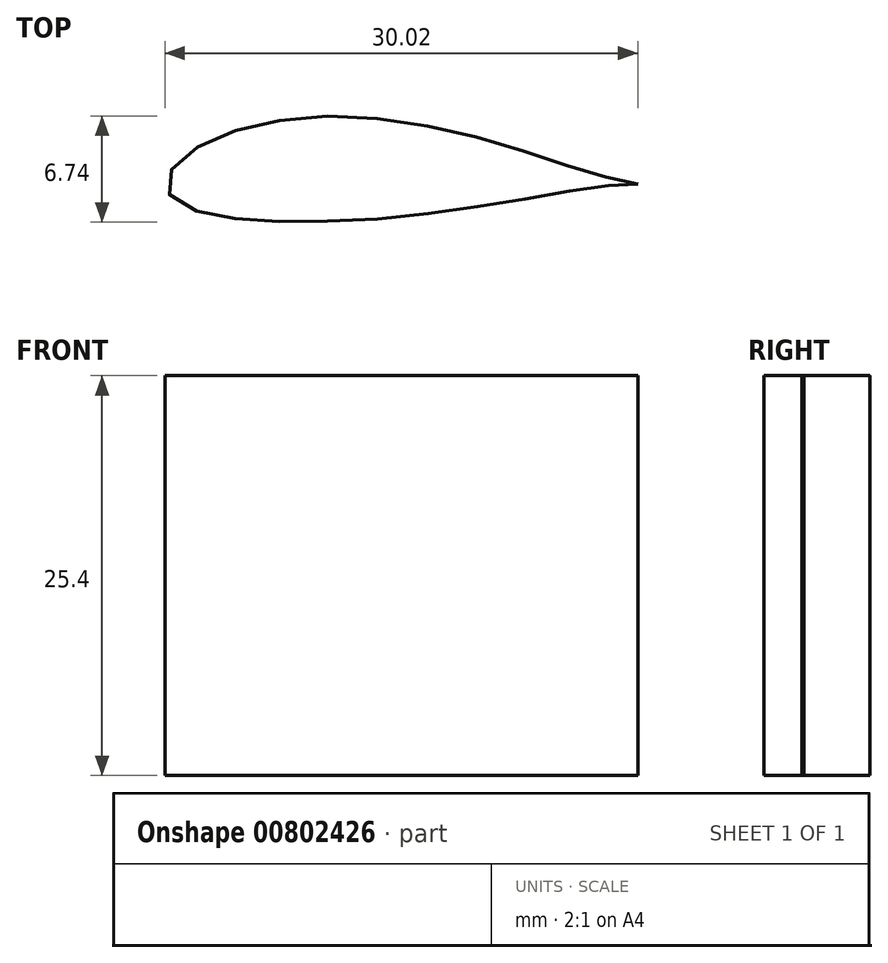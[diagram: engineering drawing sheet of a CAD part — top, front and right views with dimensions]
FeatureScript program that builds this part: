
annotation { "Feature Type Name" : "Feature", "Feature Type Description" : "" }
export const myFeature = defineFeature(function(context is Context, id is Id, definition is map)
    precondition{}
    {
        {
            var Q0;
            Q0=qCreatedBy(makeId("Top.planeOp"),FACE);
            var sketch = newSketch(context, id + "F0", { "sketchPlane" : qUnion([Q0])});
            skPoint(sketch, "E0", {"position": v(-10, 0) * mm});
            skPoint(sketch, "E1", {"position": v(-9.84, 0.56) * mm});
            skPoint(sketch, "E2", {"position": v(-9.94, 0.25) * mm});
            skPoint(sketch, "E3", {"position": v(-9.67, 0.85) * mm});
            skPoint(sketch, "E4", {"position": v(-9.46, 1.15) * mm});
            skPoint(sketch, "E5", {"position": v(-9.18, 1.45) * mm});
            skPoint(sketch, "E6", {"position": v(-8.82, 1.76) * mm});
            skPoint(sketch, "E7", {"position": v(-8.42, 2.06) * mm});
            skPoint(sketch, "E8", {"position": v(-7.96, 2.36) * mm});
            skPoint(sketch, "E9", {"position": v(-7.44, 2.63) * mm});
            skPoint(sketch, "E10", {"position": v(-6.86, 2.9) * mm});
            skPoint(sketch, "E11", {"position": v(-6.24, 3.16) * mm});
            skPoint(sketch, "E12", {"position": v(-5.55, 3.4) * mm});
            skPoint(sketch, "E13", {"position": v(-4.86, 3.6) * mm});
            skPoint(sketch, "E14", {"position": v(-4.1, 3.78) * mm});
            skPoint(sketch, "E15", {"position": v(-3.31, 3.93) * mm});
            skPoint(sketch, "E16", {"position": v(-2.48, 4.07) * mm});
            skPoint(sketch, "E17", {"position": v(-1.6, 4.18) * mm});
            skPoint(sketch, "E18", {"position": v(-0.7, 4.3) * mm});
            skPoint(sketch, "E19", {"position": v(0.21, 4.3) * mm});
            skPoint(sketch, "E20", {"position": v(1.16, 4.3) * mm});
            skPoint(sketch, "E21", {"position": v(-10, -0.27) * mm});
            skPoint(sketch, "E22", {"position": v(-9.83, -0.52) * mm});
            skPoint(sketch, "E23", {"position": v(-9.68, -0.75) * mm});
            skPoint(sketch, "E24", {"position": v(-9.46, -1) * mm});
            skPoint(sketch, "E25", {"position": v(-9.16, -1.22) * mm});
            skPoint(sketch, "E26", {"position": v(-8.82, -1.4) * mm});
            skPoint(sketch, "E27", {"position": v(-8.42, -1.6) * mm});
            skPoint(sketch, "E28", {"position": v(-7.94, -1.74) * mm});
            skPoint(sketch, "E29", {"position": v(-7.44, -1.88) * mm});
            skPoint(sketch, "E30", {"position": v(-6.85, -2.03) * mm});
            skPoint(sketch, "E31", {"position": v(-6.25, -2.14) * mm});
            skPoint(sketch, "E32", {"position": v(-5.56, -2.2) * mm});
            skPoint(sketch, "E33", {"position": v(-4.86, -2.27) * mm});
            skPoint(sketch, "E34", {"position": v(-4.1, -2.35) * mm});
            skPoint(sketch, "E35", {"position": v(1.16, -2.34) * mm});
            skPoint(sketch, "E36", {"position": v(2.1, -2.29) * mm});
            skPoint(sketch, "E37", {"position": v(4.04, 4.1) * mm});
            skPoint(sketch, "E38", {"position": v(5.04, 3.98) * mm});
            skPoint(sketch, "E39", {"position": v(6.02, 3.78) * mm});
            skPoint(sketch, "E40", {"position": v(3.08, -2.24) * mm});
            skPoint(sketch, "E41", {"position": v(4.06, -2.17) * mm});
            skPoint(sketch, "E42", {"position": v(5.04, -2.08) * mm});
            skPoint(sketch, "E43", {"position": v(6.02, -1.96) * mm});
            skPoint(sketch, "E44", {"position": v(7.02, -1.85) * mm});
            skPoint(sketch, "E45", {"position": v(7.95, -1.71) * mm});
            skPoint(sketch, "E46", {"position": v(8.91, -1.6) * mm});
            skPoint(sketch, "E47", {"position": v(9.87, -1.44) * mm});
            skPoint(sketch, "E48", {"position": v(10.78, -1.3) * mm});
            skPoint(sketch, "E49", {"position": v(11.67, -1.12) * mm});
            skPoint(sketch, "E50", {"position": v(12.53, -1) * mm});
            skPoint(sketch, "E51", {"position": v(7.02, 3.62) * mm});
            skPoint(sketch, "E52", {"position": v(7.95, 3.44) * mm});
            skPoint(sketch, "E53", {"position": v(8.93, 3.21) * mm});
            skPoint(sketch, "E54", {"position": v(9.85, 2.96) * mm});
            skPoint(sketch, "E55", {"position": v(10.76, 2.69) * mm});
            skPoint(sketch, "E56", {"position": v(11.67, 2.41) * mm});
            skPoint(sketch, "E57", {"position": v(12.53, 2.18) * mm});
            skPoint(sketch, "E58", {"position": v(13.38, 1.87) * mm});
            skPoint(sketch, "E59", {"position": v(14.15, 1.64) * mm});
            skPoint(sketch, "E60", {"position": v(13.35, -0.85) * mm});
            skPoint(sketch, "E61", {"position": v(14.16, -0.7) * mm});
            skPoint(sketch, "E62", {"position": v(14.93, -0.59) * mm});
            skPoint(sketch, "E63", {"position": v(15.62, -0.46) * mm});
            skPoint(sketch, "E64", {"position": v(16.28, -0.35) * mm});
            skPoint(sketch, "E65", {"position": v(16.93, -0.25) * mm});
            skPoint(sketch, "E66", {"position": v(17.5, -0.17) * mm});
            skPoint(sketch, "E67", {"position": v(18.01, -0.11) * mm});
            skPoint(sketch, "E68", {"position": v(20, 0) * mm});
            skPoint(sketch, "E69", {"position": v(19.88, 0) * mm});
            skPoint(sketch, "E70", {"position": v(19.72, 0) * mm});
            skPoint(sketch, "E71", {"position": v(19.52, 0) * mm});
            skPoint(sketch, "E72", {"position": v(19.2, 0) * mm});
            skPoint(sketch, "E73", {"position": v(18.47, -0.06) * mm});
            skPoint(sketch, "E74", {"position": v(18.86, -0.03) * mm});
            skPoint(sketch, "E75", {"position": v(18.86, 0.21) * mm});
            skPoint(sketch, "E76", {"position": v(19.2, 0.13) * mm});
            skPoint(sketch, "E77", {"position": v(18.47, 0.31) * mm});
            skPoint(sketch, "E78", {"position": v(19.5, 0.08) * mm});
            skPoint(sketch, "E79", {"position": v(19.72, 0.03) * mm});
            skPoint(sketch, "E80", {"position": v(19.88, 0.02) * mm});
            skPoint(sketch, "E81", {"position": v(14.9, 1.38) * mm});
            skPoint(sketch, "E82", {"position": v(15.62, 1.15) * mm});
            skPoint(sketch, "E83", {"position": v(16.28, 0.94) * mm});
            skPoint(sketch, "E84", {"position": v(16.9, 0.75) * mm});
            skPoint(sketch, "E85", {"position": v(17.5, 0.58) * mm});
            skPoint(sketch, "E86", {"position": v(18.01, 0.43) * mm});
            skPoint(sketch, "E87", {"position": v(2.1, 4.26) * mm});
            skPoint(sketch, "E88", {"position": v(3.07, 4.2) * mm});
            skPoint(sketch, "E89", {"position": v(0.2, -2.37) * mm});
            skPoint(sketch, "E90", {"position": v(-3.32, -2.37) * mm});
            skPoint(sketch, "E91", {"position": v(-2.47, -2.4) * mm});
            skPoint(sketch, "E92", {"position": v(-1.6, -2.41) * mm});
            skPoint(sketch, "E93", {"position": v(-0.7, -2.41) * mm});
            skFitSpline(sketch, "E94", {"points": [v(20, 0) * mm, v(19.88, 0.02) * mm, v(19.52, 0) * mm, v(19.2, 0) * mm, v(18.86, -0.03) * mm, v(18.47, -0.06) * mm, v(18.01, -0.11) * mm, v(17.5, -0.17) * mm, v(16.93, -0.25) * mm, v(16.28, -0.35) * mm, v(15.62, -0.46) * mm, v(14.93, -0.59) * mm, v(14.16, -0.7) * mm, v(13.35, -0.85) * mm, v(12.53, -1) * mm, v(11.67, -1.12) * mm, v(10.78, -1.3) * mm, v(9.87, -1.44) * mm, v(8.91, -1.6) * mm, v(7.95, -1.71) * mm, v(7.02, -1.85) * mm, v(6.02, -1.96) * mm, v(5.04, -2.08) * mm, v(4.06, -2.17) * mm, v(3.08, -2.24) * mm, v(2.1, -2.29) * mm, v(1.16, -2.34) * mm, v(0.2, -2.37) * mm, v(-0.7, -2.41) * mm, v(-1.6, -2.41) * mm, v(-2.47, -2.4) * mm, v(-3.32, -2.37) * mm, v(-4.1, -2.35) * mm, v(-4.86, -2.27) * mm, v(-5.56, -2.2) * mm, v(-6.25, -2.14) * mm, v(-6.85, -2.03) * mm, v(-7.44, -1.88) * mm, v(-7.94, -1.74) * mm, v(-8.42, -1.6) * mm, v(-8.82, -1.4) * mm, v(-9.16, -1.22) * mm, v(-9.46, -1) * mm, v(-9.68, -0.75) * mm, v(-9.83, -0.52) * mm, v(-10, -0.27) * mm, v(-10, 0) * mm, v(-9.94, 0.25) * mm, v(-9.84, 0.56) * mm, v(-9.67, 0.85) * mm, v(-9.46, 1.15) * mm, v(-9.18, 1.45) * mm, v(-8.82, 1.76) * mm, v(-8.42, 2.06) * mm, v(-7.96, 2.36) * mm, v(-7.44, 2.63) * mm, v(-6.86, 2.9) * mm, v(-6.24, 3.16) * mm, v(-5.55, 3.4) * mm, v(-4.86, 3.6) * mm, v(-4.1, 3.78) * mm, v(-3.31, 3.93) * mm, v(-2.48, 4.07) * mm, v(-1.6, 4.18) * mm, v(-0.7, 4.3) * mm, v(0.21, 4.3) * mm, v(1.16, 4.3) * mm, v(2.1, 4.26) * mm, v(3.07, 4.2) * mm, v(4.04, 4.1) * mm, v(5.04, 3.98) * mm, v(6.02, 3.78) * mm, v(7.02, 3.62) * mm, v(7.95, 3.44) * mm, v(8.93, 3.21) * mm, v(9.85, 2.96) * mm, v(10.76, 2.69) * mm, v(11.67, 2.41) * mm, v(12.53, 2.18) * mm, v(13.38, 1.87) * mm, v(14.15, 1.64) * mm, v(14.9, 1.38) * mm, v(15.62, 1.15) * mm, v(16.28, 0.94) * mm, v(16.9, 0.75) * mm, v(17.5, 0.58) * mm, v(18.01, 0.43) * mm, v(18.47, 0.31) * mm, v(18.86, 0.21) * mm, v(19.2, 0.13) * mm, v(19.5, 0.13) * mm, v(20, 0) * mm]});
            skSolve(sketch);
        }
        {
            var Q0;
            Q0=makeQuery(id+"F0.imprint","IMPRINT",FACE,{"disambiguationData":[TD([[makeQuery(id+"F0.imprint","IMPRINT",EDGE,{"derivedFrom":sQuery(id+"F0.wireOp",EDGE,"E94")}),-1.0]])]});
            extrude(context, id + "F1", {"entities" : qUnion([Q0]), "depth" : 25.4 * mm, "offsetDistance" : 25.4 * mm});
        }
    });
